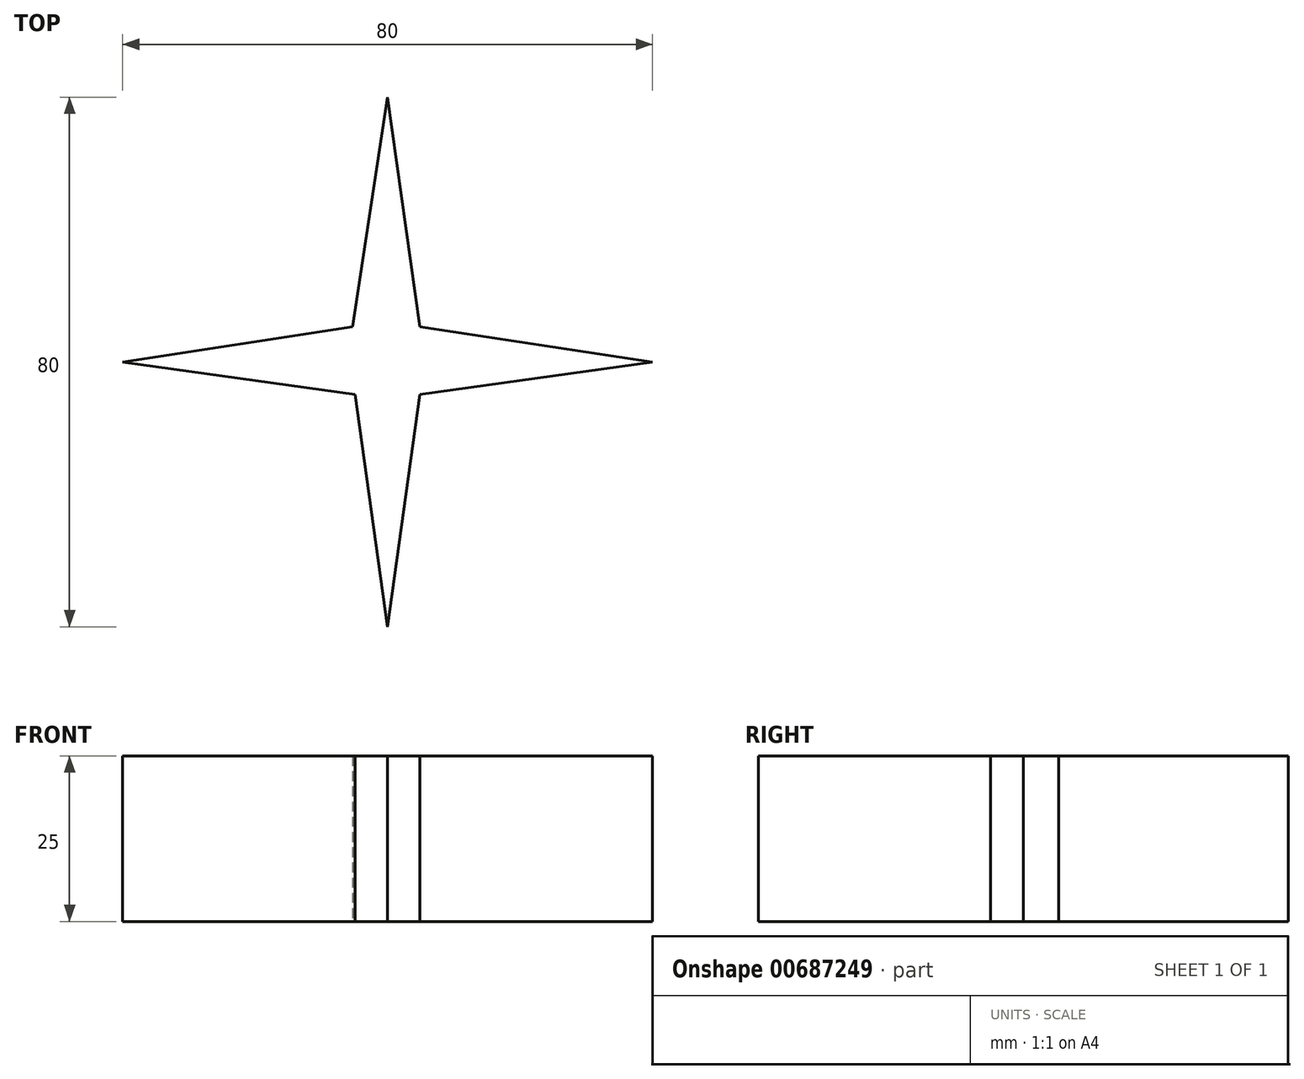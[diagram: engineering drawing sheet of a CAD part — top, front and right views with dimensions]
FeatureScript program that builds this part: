
annotation { "Feature Type Name" : "Feature", "Feature Type Description" : "" }
export const myFeature = defineFeature(function(context is Context, id is Id, definition is map)
    precondition{}
    {
        {
            var Q0;
            Q0=qCreatedBy(makeId("Top.planeOp"),FACE);
            var sketch = newSketch(context, id + "F0", { "sketchPlane" : qUnion([Q0])});
            skLineSegment(sketch, "E0", {"start": v(0, 40) * mm, "end": v(0, -40) * mm, "construction": true});
            skLineSegment(sketch, "E1", {"start": v(-40, 0) * mm, "end": v(40, 0) * mm, "construction": true});
            skLineSegment(sketch, "E2", {"start": v(0, 40) * mm, "end": v(4.86, 5.34) * mm});
            skLineSegment(sketch, "E3", {"start": v(40, 0) * mm, "end": v(4.86, 5.34) * mm});
            skLineSegment(sketch, "E4", {"start": v(40, 0) * mm, "end": v(4.86, -4.93) * mm});
            skLineSegment(sketch, "E5", {"start": v(4.86, -4.93) * mm, "end": v(0, -40) * mm});
            skLineSegment(sketch, "E6", {"start": v(0, -40) * mm, "end": v(-4.92, -4.93) * mm});
            skLineSegment(sketch, "E7", {"start": v(-4.92, -4.93) * mm, "end": v(-40, 0) * mm});
            skLineSegment(sketch, "E8", {"start": v(-40, 0) * mm, "end": v(-5.3, 5.34) * mm});
            skLineSegment(sketch, "E9", {"start": v(-5.3, 5.34) * mm, "end": v(0, 40) * mm});
            skSolve(sketch);
        }
        {
            var Q0;
            Q0=makeQuery(id+"F0.imprint","IMPRINT",FACE,{"disambiguationData":[TD([[makeQuery(id+"F0.imprint","IMPRINT",EDGE,{"derivedFrom":sQuery(id+"F0.wireOp",EDGE,"E2")}),-1.0]])]});
            extrude(context, id + "F1", {"entities" : qUnion([Q0]), "endBound" : BoundingType.SYMMETRIC, "depth" : 25 * mm, "offsetDistance" : 25 * mm});
        }
        {
            var Q0;
            Q0=makeQuery(id+"F1.opExtrude","CAP_FACE",FACE,{"disambiguationData":[OSD([sQuery(id+"F0.wireOp",EDGE,"E2"),sQuery(id+"F0.wireOp",EDGE,"E3"),sQuery(id+"F0.wireOp",EDGE,"E4"),sQuery(id+"F0.wireOp",EDGE,"E5"),sQuery(id+"F0.wireOp",EDGE,"E6"),sQuery(id+"F0.wireOp",EDGE,"E7"),sQuery(id+"F0.wireOp",EDGE,"E8"),sQuery(id+"F0.wireOp",EDGE,"E9")])],"isStart":false});
            var sketch = newSketch(context, id + "F2", { "sketchPlane" : qUnion([Q0])});
            skLineSegment(sketch, "E10", {"start": v(0, 50.34) * mm, "end": v(-54.47, -44.45) * mm});
            skSolve(sketch);
        }
    });
